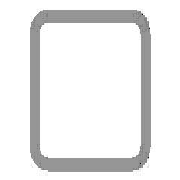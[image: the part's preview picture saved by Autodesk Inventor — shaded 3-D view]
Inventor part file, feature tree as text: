
AUTODESK INVENTOR PART (.ipt)
format: ipt  version: 2024 (Build 280153000, 153)  size: 128,512 bytes
history: native  units: mm (DEFAULTED — no unit token found)
features: other x4, extrude x1, sketch x1, plane x1
ambient origin geometry x8: Origin, YZ Plane, XZ Plane, XY Plane, X Axis, Y Axis, Z Axis, Center Point
bodies: Solid1 (feature_tree)
feature tree (7):
  parser-record x1  (decoder bookkeeping rows leaked as tree rows — omitted from the tree; the rows remain in map.json)
  other  "Driven Length"
  other  "Plano inicial"
  other  "Plano final"
  extrude  "Cuerpo"  TaperAngle=0.0deg  [1 undecoded]
  sketch  "Sketch3"  dims[d3=700.0mm d4=0.0mm d10=50.8mm d11=50.8mm d12=3.175mm d13=-0.0mm d14=700.0mm d15=25.4mm d16=25.4mm d17=6.35mm d18=90.0deg d19=700.0mm]
  plane  "Work Plane3"
note: 1 required parameter value undecoded (feature->parameter linkage not recoverable at this tier; creation-order binding heuristic only, values carry confidence <= 0.55)
